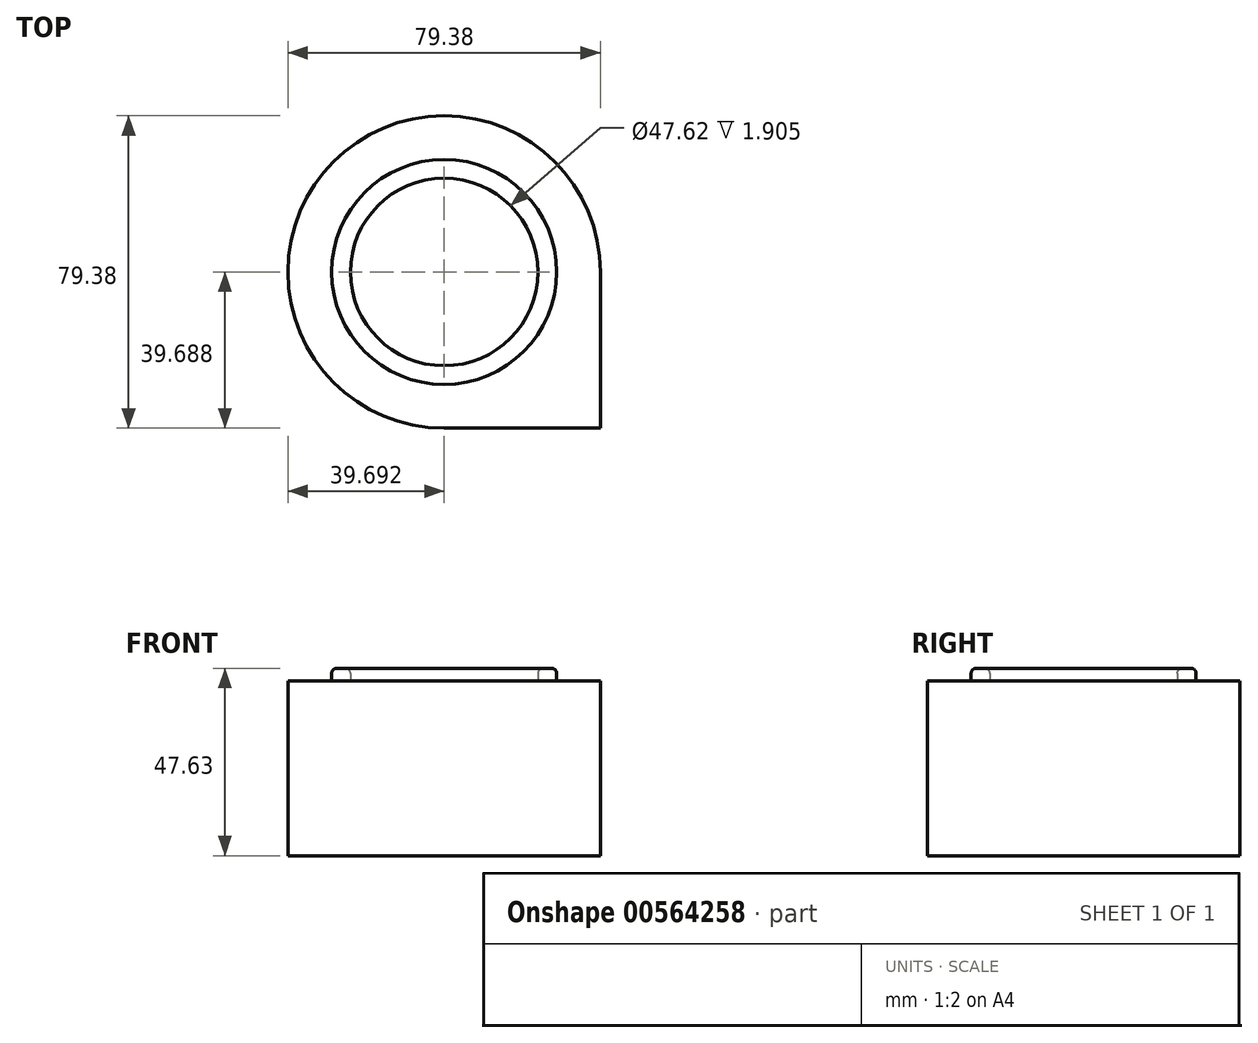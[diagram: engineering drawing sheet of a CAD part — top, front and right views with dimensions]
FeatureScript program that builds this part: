
annotation { "Feature Type Name" : "Feature", "Feature Type Description" : "" }
export const myFeature = defineFeature(function(context is Context, id is Id, definition is map)
    precondition{}
    {
        {
            var Q0;
            Q0=qCreatedBy(makeId("Top.planeOp"),FACE);
            var sketch = newSketch(context, id + "F0", { "sketchPlane" : qUnion([Q0])});
            skCircle(sketch, "E0", {"center": v(2.45, -6.71) * mm, "radius": 39.69 * mm});
            skLineSegment(sketch, "E1", {"start": v(2.45, -46.4) * mm, "end": v(42.14, -46.4) * mm});
            skLineSegment(sketch, "E2", {"start": v(42.14, -6.71) * mm, "end": v(42.14, -46.4) * mm});
            skSolve(sketch);
        }
        {
            var Q0;
            {var subQ0=sQuery(id+"F0.wireOp",EDGE,"E1");Q0=makeQuery(id+"F0.imprint","IMPRINT",FACE,{"disambiguationData":[TD([[makeQuery(id+"F0.imprint","IMPRINT",EDGE,{"derivedFrom":subQ0}),1.0]])]});}
            var Q1;
            {var subQ0=sQuery(id+"F0.wireOp",EDGE,"E0");var subQ1=makeQuery(id+"F0.imprint","INTERSECT",VERTEX,{"derivedFrom":[subQ0,sQuery(id+"F0.wireOp",EDGE,"E1")]});Q1=makeQuery(id+"F0.imprint","IMPRINT",FACE,{"disambiguationData":[TD([[makeQuery(id+"F0.imprint","IMPRINT",EDGE,{"disambiguationData":[TD([[subQ1,1.0]])],"derivedFrom":subQ0}),1.0]])]});}
            extrude(context, id + "F1", {"entities" : qUnion([Q0, Q1]), "depth" : 44.45 * mm, "offsetDistance" : 25.4 * mm});
        }
        {
            var Q0;
            Q0=makeQuery(id+"F1.opExtrude","CAP_FACE",FACE,{"disambiguationData":[OSD([sQuery(id+"F0.wireOp",EDGE,"E0"),sQuery(id+"F0.wireOp",EDGE,"E1"),sQuery(id+"F0.wireOp",EDGE,"E2")])],"isStart":false});
            var sketch = newSketch(context, id + "F2", { "sketchPlane" : qUnion([Q0])});
            skCircle(sketch, "E3", {"center": v(2.45, -6.71) * mm, "radius": 28.58 * mm});
            skCircle(sketch, "E4", {"center": v(2.45, -6.71) * mm, "radius": 23.81 * mm});
            skSolve(sketch);
        }
        {
            var Q0;
            Q0 = qSketchRegion(id + "F2", true);
            extrude(context, id + "F3", {"entities" : qUnion([Q0]), "operationType" : NewBodyOperationType.ADD, "depth" : 3.17 * mm, "offsetDistance" : 25.4 * mm});
        }
        {
            var Q0;
            Q0=makeQuery(id+"F3.opExtrude","CAP_EDGE",EDGE,{"disambiguationData":[OSD([sQuery(id+"F2.wireOp",EDGE,"E3")])],"isStart":false});
            var Q1;
            Q1=makeQuery(id+"F3.opExtrude","CAP_FACE",FACE,{"disambiguationData":[OSD([sQuery(id+"F2.wireOp",EDGE,"E3"),sQuery(id+"F2.wireOp",EDGE,"E4")])],"isStart":false});
            var Q2;
            Q2=makeQuery(id+"F3.opExtrude","CAP_EDGE",EDGE,{"disambiguationData":[OSD([sQuery(id+"F2.wireOp",EDGE,"E3")])],"isStart":true});
            var Q3;
            Q3=makeQuery(id+"F3.opExtrude","CAP_EDGE",EDGE,{"disambiguationData":[OSD([sQuery(id+"F2.wireOp",EDGE,"E4")])],"isStart":true});
            fillet(context, id + "F4", {"entities" : qUnion([Q0, Q1, Q2, Q3]), "radius" : 1.27 * mm, "tangentPropagation" : true, "allowEdgeOverflow" : false});
        }
    });
